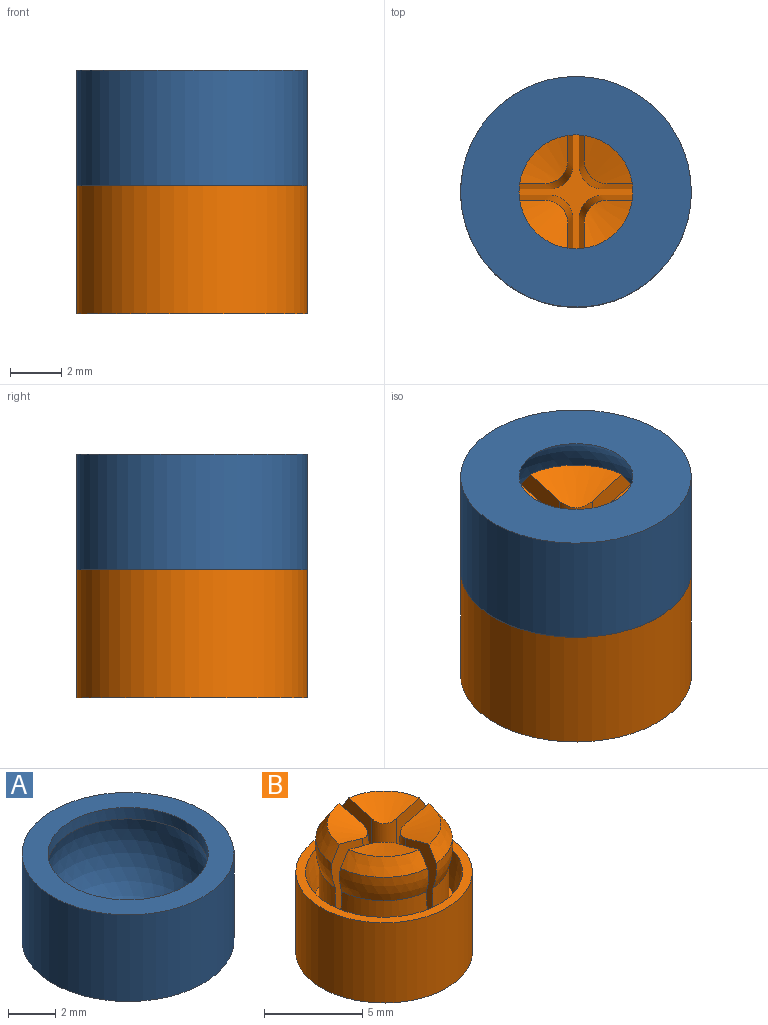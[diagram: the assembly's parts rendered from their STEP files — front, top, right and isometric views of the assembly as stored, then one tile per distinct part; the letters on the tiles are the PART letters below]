
ASSEMBLY  parts=2 mates=1
PART A: 5 faces, bbox 9x9x4.5 mm
  f0: plane 9x9mm, normal (0,0,1), area 27.3mm2, adj f2,f4
  f1: sphere r=3.58mm, area 87.7mm2, adj f2,f3
  f2: cylinder r=3.4mm len=6.8mm, axis (0,0,-1), area 12.7mm2, adj f0,f1
  f3: plane 9x9mm, normal (0,0,-1), area 48.1mm2, adj f1,f4
  f4: cylinder r=4.5mm len=9mm, axis (0,0,-1), area 127.2mm2, adj f0,f3
PART B: 33 faces, bbox 9.1x9.1x8.1 mm
  f0: sphere r=3.5mm, area 7.8mm2, adj f3,f9,f19,f20
  f1: sphere r=3.5mm, area 7.8mm2, adj f4,f10,f23,f24
  f2: sphere r=3.5mm, area 7.8mm2, adj f5,f11,f25,f26
  f3: cylinder r=3.3mm len=3.17mm, axis (0,0,-1), area 12.2mm2, adj f0,f15,f19,f20
  f4: cylinder r=3.3mm len=3.17mm, axis (0,0,-1), area 12.2mm2, adj f1,f15,f23,f24
  f5: cylinder r=3.3mm len=3.17mm, axis (0,0,-1), area 12.2mm2, adj f2,f15,f25,f26
  f6: cone r=0mm half-angle=74.6deg, axis (0,0,1), area 4.7mm2, adj f9,f19,f20,f27
  f7: cone r=0mm half-angle=74.6deg, axis (0,0,1), area 4.7mm2, adj f10,f23,f24,f30
  f8: cone r=0mm half-angle=74.6deg, axis (0,0,1), area 4.7mm2, adj f11,f25,f26,f28
  f9: cone r=2.9mm half-angle=33deg, axis (0,0,-1), area 4.6mm2, adj f0,f6,f19,f20
  f10: cone r=2.9mm half-angle=33deg, axis (0,0,-1), area 4.6mm2, adj f1,f7,f23,f24
  f11: cone r=2.9mm half-angle=33deg, axis (0,0,-1), area 4.6mm2, adj f2,f8,f25,f26
  f12: sphere r=3.5mm, area 7.8mm2, adj f16,f18,f21,f22
  f13: plane 9x9mm, normal (0,0,1), area 13.4mm2, adj f14,f32
  f14: cone r=4mm half-angle=10deg, axis (0,0,1), area 48.8mm2, adj f13,f15
  f15: plane 7.33x7.33mm, normal (0,0,1), area 11.5mm2, adj f3,f4,f5,f14,f16,f19,f20,f21
  f16: cylinder r=3.3mm len=3.17mm, axis (0,0,-1), area 12.2mm2, adj f12,f15,f21,f22
  f17: cone r=0mm half-angle=74.6deg, axis (0,0,1), area 4.7mm2, adj f18,f21,f22,f29
  f18: cone r=2.9mm half-angle=33deg, axis (0,0,-1), area 4.6mm2, adj f12,f17,f21,f22
  f19: plane 5.12x2.58mm, normal (1,0,0.04), area 10.6mm2, adj f0,f3,f6,f9,f15,f27
  f20: plane 5.12x2.58mm, normal (0,-1,0.04), area 10.6mm2, adj f0,f3,f6,f9,f15,f27
  f21: plane 5.12x2.58mm, normal (0,1,0.04), area 10.6mm2, adj f12,f15,f16,f17,f18,f29
  f22: plane 5.12x2.58mm, normal (1,0,0.04), area 10.6mm2, adj f12,f15,f16,f17,f18,f29
  f23: plane 5.12x2.58mm, normal (-1,0,0.04), area 10.6mm2, adj f1,f4,f7,f10,f15,f30
  f24: plane 5.12x2.58mm, normal (0,1,0.04), area 10.6mm2, adj f1,f4,f7,f10,f15,f30
  f25: plane 5.12x2.58mm, normal (0,-1,0.04), area 10.6mm2, adj f2,f5,f8,f11,f15,f28
  f26: plane 5.12x2.58mm, normal (-1,0,0.04), area 10.6mm2, adj f2,f5,f8,f11,f15,f28
  f27: cylinder r=0.9mm len=4.57mm, axis (-0.04,0.04,1), area 6.4mm2, adj f6,f15,f19,f20
  f28: cylinder r=0.9mm len=4.57mm, axis (0.04,0.04,1), area 6.4mm2, adj f8,f15,f25,f26
  f29: cylinder r=0.9mm len=4.57mm, axis (-0.04,-0.04,1), area 6.4mm2, adj f15,f17,f21,f22
  f30: cylinder r=0.9mm len=4.57mm, axis (0.04,-0.04,1), area 6.4mm2, adj f7,f15,f23,f24
  f31: plane 9x9mm, normal (0,0,-1), area 63.6mm2, adj f32
  f32: cylinder r=4.5mm len=9mm, axis (0,0,-1), area 141.4mm2, adj f13,f31
PLACE A rot(axis=(0.71,0.71,0),180deg) t=(-1.94,-1.87,1.13)mm
PLACE B t=(-1.94,-1.87,1.13)mm
MATE planar A.f4 <-> B.f14  axis (0,0,-1) through (-1.94,-1.87,1.13)mm
